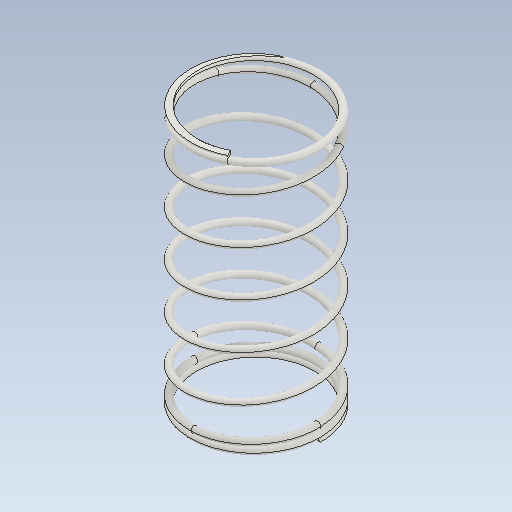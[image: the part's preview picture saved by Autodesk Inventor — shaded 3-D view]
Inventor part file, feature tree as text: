
AUTODESK INVENTOR PART (.ipt)
format: ipt  version: 2020 (Build 240168000, 168)  size: 781,312 bytes
history: native  units: mm
features: other x67, extrude x8, helix x5, sketch x3, sweep x2, plane x1
ambient origin geometry x8: Origin, YZ Plane, XZ Plane, XY Plane, X Axis, Y Axis, Z Axis, Center Point
bodies: Solid1 (feature_tree)
feature tree (86):
  other  "Main Coil Path(Right)"
  other  "Section Work Plane(Right)"
  other  "Start Work Plane(Right)"
  other  "End Work Plane(Right)"
  other  "End Cut Work Plane(Right)"
  other  "Start Cut Work Plane(Right)"
  other  "Plain Ends Cut Work Plane 1(Right)"
  other  "Plain Ends Cut Work Plane 2(Right)"
  sweep  "Main Coil Feature(R)"
  other  "Start Transition Coil 1(Right)"
  helix  "Coil  Start Transition 2(R)"  [1 undecoded]
  helix  "Coil  Start Transition 3(R)"  [1 undecoded]
  helix  "Coil  Start Transition 4(R)"  [1 undecoded]
  other  "Start Ends Coil(Right)"
  extrude  "Start Cut Feature(Right)"  Depth=10.0mm
  other  "End Transition Coil 1(Right)"
  other  "End Transition Coil 2(Right)"
  other  "End Transition Coil 3(Right)"
  other  "End Transition Coil 4(Right)"
  other  "End Coil(Right)"
  extrude  "End Cut Feature(Right)"  Depth=10.0mm
  extrude  "Plain Ends Cut Feature 1(Right)"  Depth=10.0mm
  extrude  "Plain Ends Cut  2(R)"  Depth=10.0mm TaperAngle=0.0deg
  other  "Main Coil Path(Left)"
  other  "Section Work Plane(Left)"
  other  "Start Work Plane(Left)"
  other  "End Work Plane(Left)"
  other  "End Cut Work Plane(Left)"
  other  "Start Cut Work Plane(Left)"
  other  "Plain Ends Cut Work Plane 1(Left)"
  other  "Plain Ends Cut Work Plane 2(Left)"
  sweep  "Main Coil Feature(L)"
  other  "Start Transition Coil 1(Left)"
  other  "Start Transition Coil 2(Left)"
  other  "Start Transition Coil 3(Left)"
  other  "Start Transition Coil 4(Left)"
  other  "Start Ends Coil(Left)"
  extrude  "Start Cut Feature(Left)"  Depth=10.0mm TaperAngle=0.0deg
  other  "End Transition Coil 1(Left)"
  other  "End Transition Coil 2(Left)"
  other  "End Transition Coil 3(Left)"
  other  "End Transition Coil 4(Left)"
  other  "End Coil(Left)"
  extrude  "End Cut Feature(Left)"  Depth=10.0mm
  extrude  "Cut Plain Ends Cut 1(L)"  TaperAngle=0.0deg  [1 undecoded]
  extrude  "Cut Plain Ends Cut 2(L)"  TaperAngle=0.0deg  [1 undecoded]
  other  "iMate Based Work Plane"
  other  "Preview Center Point"
  other  "Preview X Axis"
  other  "Path Section Sketch(Right)"
  other  "Srf1"
  helix  "Coil Section Sketch(Right)"  [1 undecoded]
  other  "Start Transition Coil Sketch 1(Right)"
  sketch  "Sketch  Start Transition 2(R)"  dims[d0=0.125mm d2=3.503747mm d3=10.0mm d4=45.745033mm]
  sketch  "Sketch  Start Transition 3(R)"  dims[d5=0.0mm d6=90.0deg d7=90.0deg d8=0.0mm d9=0.0mm d12=1.719816mm d13=-2.252275mm d14=0.5mm]
  sketch  "Sketch  Start Transition 4(R)"  dims[d15=0.0mm d16=2.75281mm d17=10.0mm d18=2.5mm d19=0.0mm d20=90.0deg d21=90.0deg d22=0.0mm d23=0.0mm d24=2.001874mm d25=10.0mm d26=2.5mm d27=0.0mm d28=90.0deg d29=90.0deg d30=0.0mm d31=0.0mm d32=1.250937mm d33=10.0mm d34=2.5mm d35=0.0mm d36=90.0deg d37=90.0deg d38=0.0mm d39=0.0mm d40=0.5mm d41=10.0mm d42=2.5mm d43=0.0mm d44=90.0deg d45=90.0deg d46=0.0mm d47=0.0mm d48=2.75281mm d49=10.0mm d50=1.875mm d51=0.0mm d52=90.0deg d53=90.0deg d54=0.0mm d55=0.0mm d56=2.001874mm d57=10.0mm d58=1.875mm d59=0.0mm d60=90.0deg d61=90.0deg d62=0.0mm d63=0.0mm d64=1.250937mm d65=10.0mm d66=1.875mm d67=0.0mm d68=90.0deg d69=90.0deg d70=0.0mm d71=0.0mm d72=0.5mm d73=10.0mm d74=1.875mm d75=0.0mm d76=90.0deg d77=90.0deg d78=0.0mm d79=0.0mm d81=10.0mm d82=15.0mm d83=0.0mm d84=90.0deg d85=90.0deg d86=0.0mm d87=0.0mm d88=0.503434mm d89=10.0mm d90=10.0mm d91=0.0mm d92=90.0deg d93=90.0deg d94=0.0mm d95=0.0mm d96=10.0mm d97=0.503434mm d98=0.0mm d99=10.0mm d100=0.503434mm d101=0.0mm d102=0.0mm d103=0.0mm d104=0.0mm d105=0.0mm d106=0.0mm d108=0.0mm d112=0.0mm d113=0.0mm d114=0.0mm d121=0.12928mm d131=0.0mm d132=0.0mm d133=0.0mm d134=0.0mm d135=0.125mm d137=3.503747mm d138=10.0mm d139=45.745033mm d140=0.0mm d141=90.0deg d142=90.0deg d143=0.0mm d144=0.0mm d145=1.719816mm d146=-2.252275mm d147=0.12928mm d148=0.003422mm d149=0.5mm d150=0.0mm d151=0.0mm d152=2.75281mm d153=10.0mm d154=2.5mm d155=0.0mm d156=90.0deg d157=90.0deg d158=0.0mm d159=0.0mm d160=2.001874mm d161=10.0mm d162=2.5mm d163=0.0mm d164=90.0deg d165=90.0deg d166=0.0mm d167=0.0mm d168=1.250937mm d169=10.0mm d170=2.5mm d171=0.0mm d172=90.0deg d173=90.0deg d174=0.0mm d175=0.0mm d176=0.5mm d177=10.0mm d178=2.5mm d179=0.0mm d180=90.0deg d181=90.0deg d182=0.0mm d183=0.0mm d184=10.0mm d185=10.0mm d186=10.0mm d187=10.0mm d188=0.503434mm d189=10.0mm d190=15.0mm d191=0.0mm d192=90.0deg d193=90.0deg d194=0.0mm d195=0.0mm d196=10.0mm d197=10.0mm d198=0.503434mm d199=0.0mm d200=10.0mm d201=2.75281mm d202=10.0mm d203=1.875mm d204=0.0mm d205=90.0deg d206=90.0deg d207=0.0mm d208=0.0mm d209=10.0mm d210=2.001874mm d211=10.0mm d212=1.875mm d213=0.0mm d214=90.0deg d215=90.0deg d216=0.0mm d217=0.0mm d218=1.250937mm d219=10.0mm d220=1.875mm d221=0.0mm d222=90.0deg d223=90.0deg d224=0.0mm d225=0.0mm d226=0.5mm d227=10.0mm d228=1.875mm d229=0.0mm d230=90.0deg d231=90.0deg d232=0.0mm d233=0.0mm d234=10.0mm d235=10.0mm d236=10.0mm d237=0.503434mm d238=10.0mm d239=10.0mm d240=0.0mm d241=90.0deg d242=90.0deg d243=0.0mm d244=0.0mm d245=10.0mm d246=0.503434mm d247=0.0mm d248=10.0mm d249=10.0mm d254=10.0mm d255=10.0mm d256=0.0mm d257=20.0mm d258=-0.003422mm d259=10.0mm d260=10.0mm d261=0.0mm d262=10.0mm d263=10.0mm d264=10.0mm d265=0.0mm d266=10.0mm d267=0.0mm d270=-2.189775mm d271=0.0mm d272=10.0mm d273=10.0mm d274=0.0mm d275=20.0mm d276=-157.079633mm d277=9.5mm d278=9.5mm d279=0.0mm d280=0.0mm]
  other  "End Transition Coil Sketch 1(Right)"
  other  "End Transition Coil Sketch 2(Right)"
  other  "End Transition Coil Sketch 3(Right)"
  other  "End Transition Coil Sketch 4(Right)"
  other  "Start Ends Skecth(Right)"
  other  "End Coil Skecth(Right)"
  other  "End Cut Sketch(Right)"
  other  "Start Cut Sketch(Right)"
  other  "Path Section Sketch(Left)"
  other  "Srf2"
  helix  "Coil Section Sketch(Left)"  [1 undecoded]
  other  "Start Transition Coil Sketch 1(Left)"
  other  "Start Transition Coil Sketch 2(Left)"
  other  "Start Transition Coil Sketch 3(Left)"
  other  "Start Transition Coil Sketch 4(Left)"
  other  "Start Ends Skecth(Left)"
  other  "Start Cut Sketch(Left)"
  other  "End Transition Coil Sketch 1(Left)"
  other  "End Transition Coil Sketch 2(Left)"
  other  "End Transition Coil Sketch 3(Left)"
  other  "End Transition Coil Sketch 4(Left)"
  other  "End Coil Skecth(Left)"
  other  "End Cut Sketch(Left)"
  other  "Plain Ends Cut Sketch 2(Left)"
  other  "Plain Ends Cut Sketch 2(Right)"
  other  "Plain Ends Cut Sketch 1(Right)"
  other  "Plain Ends Cut Sketch 1(Left)"
  plane  "Work Plane Start Section"
  other  "Basic Curve(Right)"
  other  "Basic Curve(Left)"
note: 7 required parameter values undecoded (feature->parameter linkage not recoverable at this tier; creation-order binding heuristic only, values carry confidence <= 0.55)
